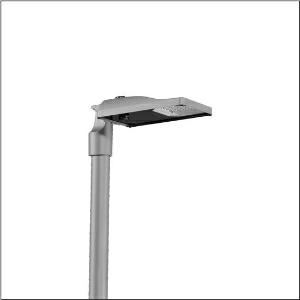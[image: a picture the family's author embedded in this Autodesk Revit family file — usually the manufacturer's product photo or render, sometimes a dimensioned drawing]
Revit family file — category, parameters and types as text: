
# Revit family: streetlight_sl_31_micro___pl52_5xh5h31t08da_3d46
name_source: partatom
category: Lighting Fixtures
units: mm (PartAtom-declared; Revit-internal decimal feet)

## family parameters
Cut with Voids When Loaded = No
Host = Face
Light Source = No
Part Type = Normal
Room Calculation Point = No
Round Connector Dimension = Use Diameter
Shared = No

## types (1)
- --- (1 x LED, 4850 lm, 37.7 W, 3000K)
    Apparent Load = 38 VA
    CIE Flux Codes = 27 59 98 100 100
    Color Rendering = 70
    Color Temperature = 3000K
    Default Elevation = 1800 mm
    Description = Streetlight SL 31 micro, mast luminaire, primary light control with lens, of PMMA, primary optical cover: cover, of toughened safety glass, transparent, light distribution: PL52, light emission: direct distribution, primary light characteristic: asymmetric, installation type: post-top, side-entry, LED, High Power LED, rated luminous flux: 4.850lm, luminous efficacy: 129lm/W, light colour: 730, colour temperature: 3000K, control: presetting dimming logarithmic, flexible luminous flux parameterisation, time-dependent luminous flux control, constant luminous flux control, power reduction, intelligent temperature release in ECG and LED module, overheat protection, with cable H07RN-F 2x 1.5mm², mains connection: 220..240V, AC, 50/60Hz, connection cable pre-assembled, cable length: 6,5m, start of lifetime: 38W, end of service life: 41W, reduction: 16W, luminaire housing, of diecast aluminium, powder-coated, Siteco® metallic grey (DB 702S), corrosivity category C5 high according to DIN EN ISO 12944, sealing non-destructively replaceable, multi-level sealing system, mast flange (76/60mm) included as standard, inclination: -15°..+20° (post-top) | -20°..+20° (side-entry), adjustable in 5° steps, no sealing on luminaire upper side, Smart Interface below and above, protection rating (complete): IP66, insulation class (complete): insulation class II (safety insulation), certification: CE, ENEC, ENEC+, VDE, UKCA, ZD4i, impact resistance: IK09, permissible operating ambient temperature for outdoor applications: -40..+50°C, standard-compliant lighting for roads and squares, packaging unit: 1 piece

Light Distribution: PL52
    Height = 76 mm
    Lamp = 1 x LED
    Lamp Light Flux = 4850 lm
    Lamp Power = 37.7 W
    Lamp count = 1
    Length = 467 mm
    Luminous efficacy = 129 lm/W
    Manufacturer = Siteco
    ModVariant = No
    Model = 5XH5H31T08DA
    Number of Poles = 1
    OnlyDefault = Yes
    Power Factor = 1
    Product Name = Streetlight SL 31 micro | PL52
    Product group = mast luminaire | pylon top
    ProductGroupID = 6100
    Protection Class = Protection class II
    Protection Degree = IP 66
    RLX_Detail_Level = 1
    RLX_Emergency_Light_Flux = 0 lm
    RLX_Emergency_Type = 0
    RLX_Emergency_Type_DB = No
    RlxData = <blob elided: 54045 chars, md5=3312aa61>
    Socket = socket
    Standby Power = 0 W
    System Light Flux = 4850 lm
    System Power = 38 W
    Type Comments = factory setting: luminous flux: 100 % | dim-lin: 254 | 745 mA
    Type Image = l_1300315.jpg
    URL = http://relux.com
    VarID = @adj_006135
    Voltage = 0 V
    Weight = 0.00 kg
    Width = 265 mm

## geometry (parser evidence)
native form markers: Blend x4, Sweep x11
no freeform markers — native parametric forms only
